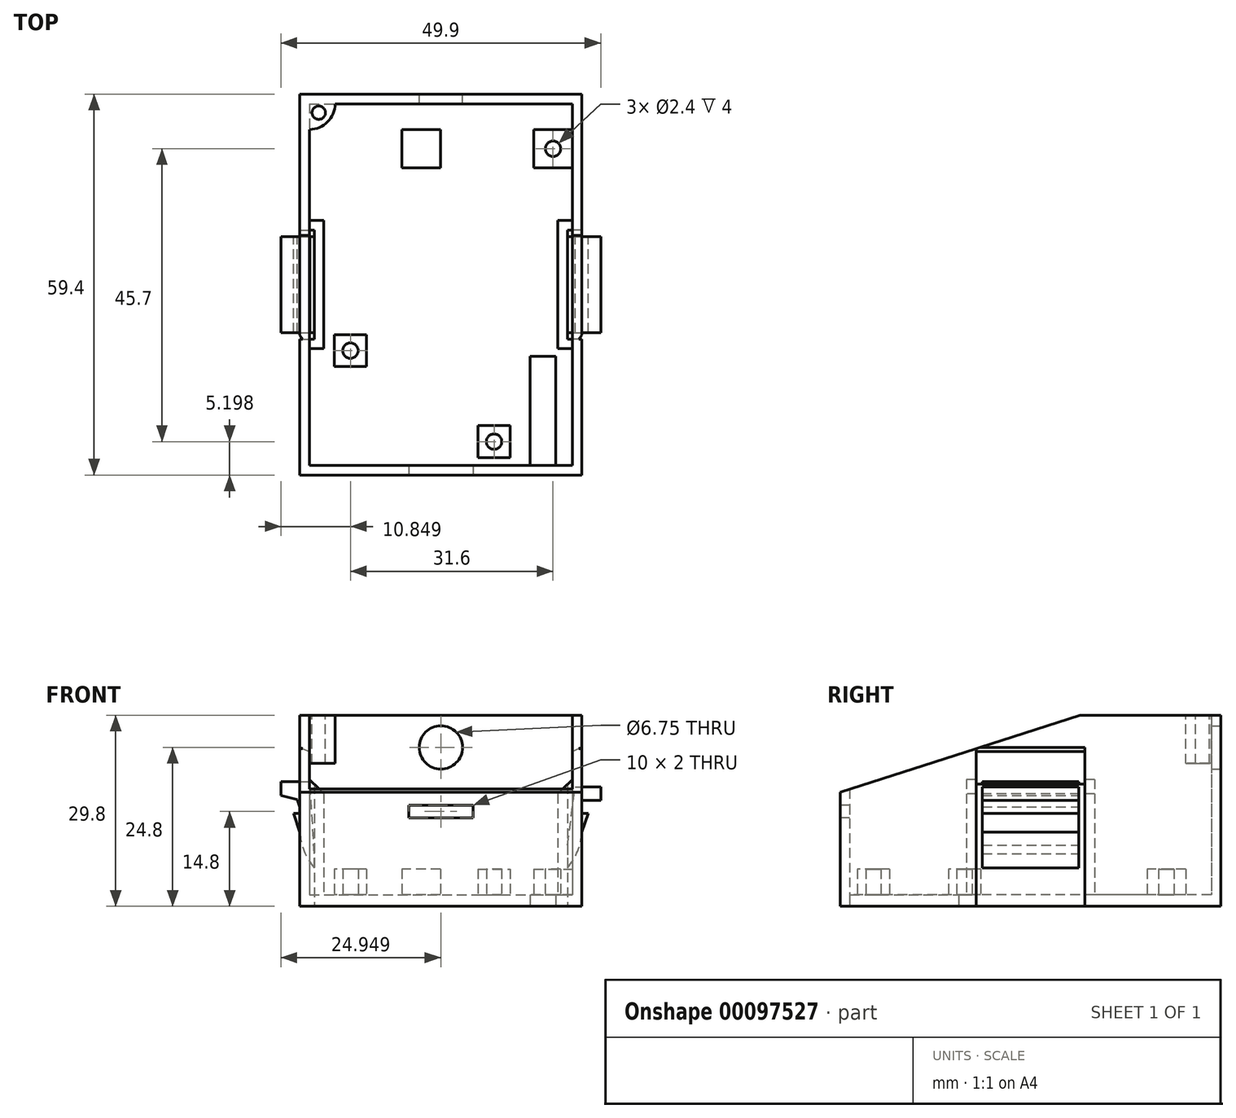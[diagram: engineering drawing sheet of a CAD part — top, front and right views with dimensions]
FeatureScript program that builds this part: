
annotation { "Feature Type Name" : "Feature", "Feature Type Description" : "" }
export const myFeature = defineFeature(function(context is Context, id is Id, definition is map)
    precondition{}
    {
        {
            var Q0;
            Q0=qCreatedBy(makeId("Top.planeOp"),FACE);
            var sketch = newSketch(context, id + "F0", { "sketchPlane" : qUnion([Q0])});
            skLineSegment(sketch, "E0.bottom", {"start": v(-56.63, 54.28) * mm, "end": v(-12.63, 54.28) * mm});
            skLineSegment(sketch, "E0.top", {"start": v(-56.63, -5.12) * mm, "end": v(-12.63, -5.12) * mm});
            skCircle(sketch, "E1", {"center": v(-12.63, -5.12) * mm, "radius": 1.5 * mm, "construction": true});
            skCircle(sketch, "E2", {"center": v(-56.63, -5.12) * mm, "radius": 1.5 * mm, "construction": true});
            skLineSegment(sketch, "E3", {"start": v(-56.63, -3.62) * mm, "end": v(-12.63, -3.62) * mm, "construction": true});
            skCircle(sketch, "E4", {"center": v(-12.63, -3.62) * mm, "radius": 4.1 * mm, "construction": true});
            skLineSegment(sketch, "E5.bottom", {"start": v(-16.73, -3.62) * mm, "end": v(-20.73, -3.62) * mm});
            skLineSegment(sketch, "E5.top", {"start": v(-16.73, 13.38) * mm, "end": v(-20.73, 13.38) * mm});
            skLineSegment(sketch, "E5.left", {"start": v(-16.73, -3.62) * mm, "end": v(-16.73, 13.38) * mm});
            skLineSegment(sketch, "E5.right", {"start": v(-20.73, -3.62) * mm, "end": v(-20.73, 13.38) * mm});
            skLineSegment(sketch, "E6", {"start": v(-56.63, 24.58) * mm, "end": v(-12.63, 24.58) * mm, "construction": true});
            skCircle(sketch, "E7", {"center": v(-56.63, 24.58) * mm, "radius": 8.5 * mm, "construction": true});
            skLineSegment(sketch, "E8", {"start": v(-56.63, 33.08) * mm, "end": v(-54.38, 33.08) * mm});
            skLineSegment(sketch, "E9", {"start": v(-56.63, 16.08) * mm, "end": v(-54.38, 16.08) * mm});
            skLineSegment(sketch, "E10", {"start": v(-54.38, 33.08) * mm, "end": v(-54.38, 16.08) * mm});
            skLineSegment(sketch, "E11", {"start": v(-56.63, 54.28) * mm, "end": v(-56.63, 33.08) * mm});
            skLineSegment(sketch, "E12", {"start": v(-56.63, 16.08) * mm, "end": v(-56.63, -5.12) * mm});
            skLineSegment(sketch, "E13", {"start": v(-34.63, 54.28) * mm, "end": v(-34.63, 40.65) * mm, "construction": true});
            skLineSegment(sketch, "E14.MirrorCS", {"start": v(-12.63, 16.08) * mm, "end": v(-12.63, -5.12) * mm});
            skLineSegment(sketch, "E15.MirrorCS", {"start": v(-12.63, 16.08) * mm, "end": v(-14.88, 16.08) * mm});
            skLineSegment(sketch, "E16.MirrorCS", {"start": v(-12.63, 33.08) * mm, "end": v(-14.88, 33.08) * mm});
            skLineSegment(sketch, "E17.MirrorCS", {"start": v(-12.63, 54.28) * mm, "end": v(-12.63, 33.08) * mm});
            skLineSegment(sketch, "E18.MirrorCS", {"start": v(-14.88, 33.08) * mm, "end": v(-14.88, 16.08) * mm});
            skSolve(sketch);
        }
        {
            var Q0;
            Q0=makeQuery(id+"F0.imprint","IMPRINT",FACE,{"disambiguationData":[TD([[makeQuery(id+"F0.imprint","IMPRINT",EDGE,{"derivedFrom":sQuery(id+"F0.wireOp",EDGE,"E0.bottom")}),-1.0]])]});
            extrude(context, id + "F1", {"entities" : qUnion([Q0]), "depth" : 1.8 * mm});
        }
        {
            var Q0;
            Q0=makeQuery(id+"F1.opExtrude","CAP_FACE",FACE,{"disambiguationData":[OSD([sQuery(id+"F0.wireOp",EDGE,"E0.bottom"),sQuery(id+"F0.wireOp",EDGE,"E0.top"),sQuery(id+"F0.wireOp",EDGE,"E5.bottom"),sQuery(id+"F0.wireOp",EDGE,"E5.top"),sQuery(id+"F0.wireOp",EDGE,"E5.left"),sQuery(id+"F0.wireOp",EDGE,"E5.right"),sQuery(id+"F0.wireOp",EDGE,"E8"),sQuery(id+"F0.wireOp",EDGE,"E9"),sQuery(id+"F0.wireOp",EDGE,"E10"),sQuery(id+"F0.wireOp",EDGE,"E11"),sQuery(id+"F0.wireOp",EDGE,"E12"),sQuery(id+"F0.wireOp",EDGE,"E14.MirrorCS"),sQuery(id+"F0.wireOp",EDGE,"E15.MirrorCS"),sQuery(id+"F0.wireOp",EDGE,"E16.MirrorCS"),sQuery(id+"F0.wireOp",EDGE,"E17.MirrorCS"),sQuery(id+"F0.wireOp",EDGE,"E18.MirrorCS")])],"isStart":false});
            var sketch = newSketch(context, id + "F2", { "sketchPlane" : qUnion([Q0])});
            skLineSegment(sketch, "E19.0", {"start": v(-55.13, 52.78) * mm, "end": v(-55.13, 34.58) * mm});
            skLineSegment(sketch, "E19.1", {"start": v(-14.13, 14.58) * mm, "end": v(-16.38, 14.58) * mm});
            skLineSegment(sketch, "E19.2", {"start": v(-16.38, 34.58) * mm, "end": v(-16.38, 14.58) * mm});
            skLineSegment(sketch, "E19.3", {"start": v(-14.13, 34.58) * mm, "end": v(-16.38, 34.58) * mm});
            skLineSegment(sketch, "E19.4", {"start": v(-14.13, 52.78) * mm, "end": v(-14.13, 34.58) * mm});
            skLineSegment(sketch, "E19.5", {"start": v(-14.13, 14.58) * mm, "end": v(-14.13, -3.62) * mm});
            skLineSegment(sketch, "E19.6", {"start": v(-55.13, 52.78) * mm, "end": v(-14.13, 52.78) * mm});
            skLineSegment(sketch, "E19.7", {"start": v(-55.13, -3.62) * mm, "end": v(-14.13, -3.62) * mm});
            skLineSegment(sketch, "E19.8", {"start": v(-55.13, 14.58) * mm, "end": v(-55.13, -3.62) * mm});
            skLineSegment(sketch, "E19.9", {"start": v(-55.13, 14.58) * mm, "end": v(-52.88, 14.58) * mm});
            skLineSegment(sketch, "E19.10", {"start": v(-52.88, 34.58) * mm, "end": v(-52.88, 14.58) * mm});
            skLineSegment(sketch, "E19.11", {"start": v(-55.13, 34.58) * mm, "end": v(-52.88, 34.58) * mm});
            skSolve(sketch);
        }
        {
            var Q0;
            Q0=makeQuery(id+"F2.imprint","IMPRINT",FACE,{"disambiguationData":[TD([[makeQuery(id+"F2.imprint","IMPRINT",EDGE,{"derivedFrom":sQuery(id+"F2.wireOp",EDGE,"E19.0")}),-1.0]])]});
            extrude(context, id + "F3", {"entities" : qUnion([Q0]), "operationType" : NewBodyOperationType.ADD, "depth" : 22 * mm});
        }
        {
            var Q0;
            Q0=makeQuery(id+"F3.opExtrude","CAP_FACE",FACE,{"disambiguationData":[OSD([sQuery(id+"F0.wireOp",EDGE,"E0.bottom"),sQuery(id+"F0.wireOp",EDGE,"E0.top"),sQuery(id+"F0.wireOp",EDGE,"E8"),sQuery(id+"F0.wireOp",EDGE,"E9"),sQuery(id+"F0.wireOp",EDGE,"E10"),sQuery(id+"F0.wireOp",EDGE,"E11"),sQuery(id+"F0.wireOp",EDGE,"E12"),sQuery(id+"F0.wireOp",EDGE,"E14.MirrorCS"),sQuery(id+"F0.wireOp",EDGE,"E15.MirrorCS"),sQuery(id+"F0.wireOp",EDGE,"E16.MirrorCS"),sQuery(id+"F0.wireOp",EDGE,"E17.MirrorCS"),sQuery(id+"F0.wireOp",EDGE,"E18.MirrorCS"),sQuery(id+"F2.wireOp",EDGE,"E19.0"),sQuery(id+"F2.wireOp",EDGE,"E19.1"),sQuery(id+"F2.wireOp",EDGE,"E19.2"),sQuery(id+"F2.wireOp",EDGE,"E19.3"),sQuery(id+"F2.wireOp",EDGE,"E19.4"),sQuery(id+"F2.wireOp",EDGE,"E19.5"),sQuery(id+"F2.wireOp",EDGE,"E19.6"),sQuery(id+"F2.wireOp",EDGE,"E19.7"),sQuery(id+"F2.wireOp",EDGE,"E19.8"),sQuery(id+"F2.wireOp",EDGE,"E19.9"),sQuery(id+"F2.wireOp",EDGE,"E19.10"),sQuery(id+"F2.wireOp",EDGE,"E19.11")])],"isStart":false});
            var sketch = newSketch(context, id + "F4", { "sketchPlane" : qUnion([Q0])});
            skLineSegment(sketch, "E20.bottom", {"start": v(-56.63, 54.28) * mm, "end": v(-12.63, 54.28) * mm});
            skLineSegment(sketch, "E20.top", {"start": v(-56.63, -5.12) * mm, "end": v(-12.63, -5.12) * mm});
            skLineSegment(sketch, "E20.left", {"start": v(-56.63, 54.28) * mm, "end": v(-56.63, -5.12) * mm});
            skLineSegment(sketch, "E20.right", {"start": v(-12.63, 54.28) * mm, "end": v(-12.63, -5.12) * mm});
            skLineSegment(sketch, "E21.bottom", {"start": v(-55.13, 52.78) * mm, "end": v(-14.13, 52.78) * mm});
            skLineSegment(sketch, "E21.top", {"start": v(-55.13, -3.62) * mm, "end": v(-14.13, -3.62) * mm});
            skLineSegment(sketch, "E22", {"start": v(-14.13, 52.78) * mm, "end": v(-55.13, 52.78) * mm});
            skLineSegment(sketch, "E23", {"start": v(-55.13, 52.78) * mm, "end": v(-55.13, 34.58) * mm});
            skLineSegment(sketch, "E24", {"start": v(-55.13, 34.58) * mm, "end": v(-52.88, 34.58) * mm});
            skLineSegment(sketch, "E25", {"start": v(-52.88, 34.58) * mm, "end": v(-52.88, 14.58) * mm});
            skLineSegment(sketch, "E26", {"start": v(-52.88, 14.58) * mm, "end": v(-55.13, 14.58) * mm});
            skLineSegment(sketch, "E27", {"start": v(-55.13, 14.58) * mm, "end": v(-55.13, -3.62) * mm});
            skLineSegment(sketch, "E28", {"start": v(-14.13, -3.62) * mm, "end": v(-14.13, 14.58) * mm});
            skLineSegment(sketch, "E29", {"start": v(-14.13, 14.58) * mm, "end": v(-16.38, 14.58) * mm});
            skLineSegment(sketch, "E30", {"start": v(-16.38, 14.58) * mm, "end": v(-16.38, 34.58) * mm});
            skLineSegment(sketch, "E31", {"start": v(-16.38, 34.58) * mm, "end": v(-14.13, 34.58) * mm});
            skLineSegment(sketch, "E32", {"start": v(-14.13, 34.58) * mm, "end": v(-14.13, 52.78) * mm});
            skSolve(sketch);
        }
        {
            var Q0;
            Q0=qSketchRegion(id+"F4",true);
            extrude(context, id + "F5", {"entities" : qUnion([Q0]), "operationType" : NewBodyOperationType.ADD, "depth" : 6 * mm});
        }
        {
            var Q0;
            Q0=makeQuery(id+"F5.opExtrude","CAP_FACE",FACE,{"disambiguationData":[OSD([sQuery(id+"F4.wireOp",EDGE,"E20.bottom"),sQuery(id+"F4.wireOp",EDGE,"E20.top"),sQuery(id+"F4.wireOp",EDGE,"E20.left"),sQuery(id+"F4.wireOp",EDGE,"E20.right"),sQuery(id+"F4.wireOp",EDGE,"E21.top"),sQuery(id+"F4.wireOp",EDGE,"E22"),sQuery(id+"F4.wireOp",EDGE,"E23"),sQuery(id+"F4.wireOp",EDGE,"E24"),sQuery(id+"F4.wireOp",EDGE,"E25"),sQuery(id+"F4.wireOp",EDGE,"E26"),sQuery(id+"F4.wireOp",EDGE,"E27"),sQuery(id+"F4.wireOp",EDGE,"E28"),sQuery(id+"F4.wireOp",EDGE,"E29"),sQuery(id+"F4.wireOp",EDGE,"E30"),sQuery(id+"F4.wireOp",EDGE,"E31"),sQuery(id+"F4.wireOp",EDGE,"E32")])],"isStart":false});
            var sketch = newSketch(context, id + "F6", { "sketchPlane" : qUnion([Q0])});
            skLineSegment(sketch, "E33.bottom", {"start": v(-55.13, 34.58) * mm, "end": v(-52.88, 34.58) * mm});
            skLineSegment(sketch, "E33.top", {"start": v(-55.13, 14.58) * mm, "end": v(-52.88, 14.58) * mm});
            skLineSegment(sketch, "E33.left", {"start": v(-55.13, 34.58) * mm, "end": v(-55.13, 14.58) * mm});
            skLineSegment(sketch, "E33.right", {"start": v(-52.88, 34.58) * mm, "end": v(-52.88, 14.58) * mm});
            skLineSegment(sketch, "E34.bottom", {"start": v(-16.38, 34.58) * mm, "end": v(-14.13, 34.58) * mm});
            skLineSegment(sketch, "E34.top", {"start": v(-16.38, 14.58) * mm, "end": v(-14.13, 14.58) * mm});
            skLineSegment(sketch, "E34.left", {"start": v(-16.38, 34.58) * mm, "end": v(-16.38, 14.58) * mm});
            skLineSegment(sketch, "E34.right", {"start": v(-14.13, 34.58) * mm, "end": v(-14.13, 14.58) * mm});
            skSolve(sketch);
        }
        {
            var Q0;
            Q0=qSketchRegion(id+"F6",true);
            extrude(context, id + "F7", {"entities" : qUnion([Q0]), "operationType" : NewBodyOperationType.REMOVE, "oppositeDirection" : true, "depth" : 10 * mm});
        }
        {
            var Q0;
            Q0=makeQuery(id+"F5.boolean.opBoolean","MERGE",FACE,{"derivedFrom":[makeQuery(id+"F3.opExtrude","SWEPT_FACE",FACE,{"disambiguationData":[OSD([sQuery(id+"F2.wireOp",EDGE,"E19.9")])]}),makeQuery(id+"F5.opExtrude","SWEPT_FACE",FACE,{"disambiguationData":[OSD([sQuery(id+"F4.wireOp",EDGE,"E26")])]})]});
            var sketch = newSketch(context, id + "F8", { "sketchPlane" : qUnion([Q0])});
            skLineSegment(sketch, "E35", {"start": v(-55.13, 19.8) * mm, "end": v(-52.88, 17.55) * mm});
            skLineSegment(sketch, "E36", {"start": v(-52.88, 17.55) * mm, "end": v(-52.88, 19.8) * mm});
            skLineSegment(sketch, "E37", {"start": v(-52.88, 19.8) * mm, "end": v(-55.13, 19.8) * mm});
            skSolve(sketch);
        }
        {
            var Q0;
            Q0=makeQuery(id+"F8.imprint","IMPRINT",FACE,{"disambiguationData":[TD([[makeQuery(id+"F8.imprint","IMPRINT",EDGE,{"derivedFrom":sQuery(id+"F8.wireOp",EDGE,"E35")}),1.0]])]});
            extrude(context, id + "F9", {"entities" : qUnion([Q0]), "operationType" : NewBodyOperationType.REMOVE, "oppositeDirection" : true, "depth" : 20 * mm});
        }
        {
            var Q0;
            {var subQ0=sQuery(id+"F0.wireOp",EDGE,"E8");Q0=makeQuery(id+"F3.boolean.opBoolean","MERGE",FACE,{"derivedFrom":[makeQuery(id+"F1.opExtrude","SWEPT_FACE",FACE,{"disambiguationData":[OSD([subQ0])]}),makeQuery(id+"F3.opExtrude","SWEPT_FACE",FACE,{"disambiguationData":[OSD([subQ0])]})]});}
            var sketch = newSketch(context, id + "F10", { "sketchPlane" : qUnion([Q0])});
            skLineSegment(sketch, "E38", {"start": v(-56.63, 23.8) * mm, "end": v(-54.38, 23.8) * mm});
            skLineSegment(sketch, "E39", {"start": v(-56.63, 23.8) * mm, "end": v(-56.63, 24.8) * mm});
            skLineSegment(sketch, "E40", {"start": v(-56.63, 23.8) * mm, "end": v(-55.88, 23.8) * mm});
            skCircle(sketch, "E41", {"center": v(-56.63, 23.8) * mm, "radius": 2 * mm, "construction": true});
            skLineSegment(sketch, "E42", {"start": v(-56.63, 24.8) * mm, "end": v(-54.38, 23.8) * mm});
            skSolve(sketch);
        }
        {
            var Q0;
            Q0=qSketchRegion(id+"F10",true);
            extrude(context, id + "F11", {"entities" : qUnion([Q0]), "operationType" : NewBodyOperationType.REMOVE, "depth" : 17 * mm});
        }
        {
            var Q0;
            Q0=makeQuery(id+"F5.boolean.opBoolean","MERGE",FACE,{"derivedFrom":[makeQuery(id+"F3.opExtrude","SWEPT_FACE",FACE,{"disambiguationData":[OSD([sQuery(id+"F2.wireOp",EDGE,"E19.3")])]}),makeQuery(id+"F5.opExtrude","SWEPT_FACE",FACE,{"disambiguationData":[OSD([sQuery(id+"F4.wireOp",EDGE,"E31")])]})]});
            var sketch = newSketch(context, id + "F12", { "sketchPlane" : qUnion([Q0])});
            skLineSegment(sketch, "E43", {"start": v(16.38, 19.8) * mm, "end": v(14.13, 19.8) * mm});
            skLineSegment(sketch, "E44", {"start": v(14.13, 19.8) * mm, "end": v(16.38, 17.55) * mm});
            skLineSegment(sketch, "E45", {"start": v(16.38, 17.55) * mm, "end": v(16.38, 19.8) * mm});
            skSolve(sketch);
        }
        {
            var Q0;
            Q0=qSketchRegion(id+"F12",true);
            extrude(context, id + "F13", {"entities" : qUnion([Q0]), "operationType" : NewBodyOperationType.REMOVE, "oppositeDirection" : true, "depth" : 20 * mm});
        }
        {
            var Q0;
            {var subQ0=sQuery(id+"F0.wireOp",EDGE,"E15.MirrorCS");Q0=makeQuery(id+"F3.boolean.opBoolean","MERGE",FACE,{"derivedFrom":[makeQuery(id+"F1.opExtrude","SWEPT_FACE",FACE,{"disambiguationData":[OSD([subQ0])]}),makeQuery(id+"F3.opExtrude","SWEPT_FACE",FACE,{"disambiguationData":[OSD([subQ0])]})]});}
            var sketch = newSketch(context, id + "F14", { "sketchPlane" : qUnion([Q0])});
            skLineSegment(sketch, "E46", {"start": v(12.63, 23.8) * mm, "end": v(12.63, 24.8) * mm});
            skLineSegment(sketch, "E47", {"start": v(12.63, 24.8) * mm, "end": v(14.88, 23.8) * mm});
            skLineSegment(sketch, "E48", {"start": v(14.88, 23.8) * mm, "end": v(12.63, 23.8) * mm});
            skSolve(sketch);
        }
        {
            var Q0;
            Q0=qSketchRegion(id+"F14",true);
            extrude(context, id + "F15", {"entities" : qUnion([Q0]), "operationType" : NewBodyOperationType.REMOVE, "depth" : 17 * mm});
        }
        {
            var Q0;
            {var subQ0=sQuery(id+"F0.wireOp",EDGE,"E17.MirrorCS");var subQ1=sQuery(id+"F0.wireOp",EDGE,"E14.MirrorCS");Q0=makeQuery(id+"F5.boolean.opBoolean","MERGE",FACE,{"derivedFrom":[makeQuery(id+"F3.boolean.opBoolean","MERGE",FACE,{"derivedFrom":[makeQuery(id+"F1.opExtrude","SWEPT_FACE",FACE,{"disambiguationData":[OSD([subQ1])]}),makeQuery(id+"F3.opExtrude","SWEPT_FACE",FACE,{"disambiguationData":[OSD([subQ1])]})]}),makeQuery(id+"F3.boolean.opBoolean","MERGE",FACE,{"derivedFrom":[makeQuery(id+"F1.opExtrude","SWEPT_FACE",FACE,{"disambiguationData":[OSD([subQ0])]}),makeQuery(id+"F3.opExtrude","SWEPT_FACE",FACE,{"disambiguationData":[OSD([subQ0])]})]}),makeQuery(id+"F5.opExtrude","SWEPT_FACE",FACE,{"disambiguationData":[OSD([sQuery(id+"F4.wireOp",EDGE,"E20.right")])]})]});}
            var sketch = newSketch(context, id + "F16", { "sketchPlane" : qUnion([Q0])});
            skCircle(sketch, "E49", {"center": v(-5.12, 29.8) * mm, "radius": 12 * mm, "construction": true});
            skCircle(sketch, "E50", {"center": v(54.28, 29.8) * mm, "radius": 22 * mm, "construction": true});
            skLineSegment(sketch, "E51", {"start": v(-5.12, 29.8) * mm, "end": v(-5.12, 17.8) * mm});
            skLineSegment(sketch, "E52", {"start": v(-5.12, 17.8) * mm, "end": v(32.28, 29.8) * mm});
            skLineSegment(sketch, "E53", {"start": v(32.28, 29.8) * mm, "end": v(-5.12, 29.8) * mm});
            skCircle(sketch, "E54", {"center": v(54.28, 29.8) * mm, "radius": 10 * mm, "construction": true});
            skLineSegment(sketch, "E55", {"start": v(44.28, 29.8) * mm, "end": v(44.28, 23.8) * mm, "construction": true});
            skCircle(sketch, "E56", {"center": v(44.28, 23.8) * mm, "radius": 3.38 * mm, "construction": true});
            skSolve(sketch);
        }
        {
            var Q0;
            Q0=qSketchRegion(id+"F16",true);
            extrude(context, id + "F17", {"entities" : qUnion([Q0]), "operationType" : NewBodyOperationType.REMOVE, "oppositeDirection" : true, "depth" : 45 * mm});
        }
        {
            var Q0;
            {var subQ0=sQuery(id+"F0.wireOp",EDGE,"E0.bottom");Q0=makeQuery(id+"F5.boolean.opBoolean","MERGE",FACE,{"derivedFrom":[makeQuery(id+"F3.boolean.opBoolean","MERGE",FACE,{"derivedFrom":[makeQuery(id+"F1.opExtrude","SWEPT_FACE",FACE,{"disambiguationData":[OSD([subQ0])]}),makeQuery(id+"F3.opExtrude","SWEPT_FACE",FACE,{"disambiguationData":[OSD([subQ0])]})]}),makeQuery(id+"F5.opExtrude","SWEPT_FACE",FACE,{"disambiguationData":[OSD([sQuery(id+"F4.wireOp",EDGE,"E20.bottom")])]})]});}
            var sketch = newSketch(context, id + "F18", { "sketchPlane" : qUnion([Q0])});
            skLineSegment(sketch, "E57", {"start": v(34.63, 29.8) * mm, "end": v(34.63, 24.8) * mm, "construction": true});
            skCircle(sketch, "E58", {"center": v(34.63, 24.8) * mm, "radius": 3.38 * mm});
            skSolve(sketch);
        }
        {
            var Q0;
            Q0=qSketchRegion(id+"F18",true);
            extrude(context, id + "F19", {"entities" : qUnion([Q0]), "operationType" : NewBodyOperationType.REMOVE, "oppositeDirection" : true, "depth" : 3 * mm});
        }
        {
            var Q0;
            Q0=makeQuery(id+"F5.opExtrude","CAP_FACE",FACE,{"disambiguationData":[OSD([sQuery(id+"F4.wireOp",EDGE,"E20.bottom"),sQuery(id+"F4.wireOp",EDGE,"E20.top"),sQuery(id+"F4.wireOp",EDGE,"E20.left"),sQuery(id+"F4.wireOp",EDGE,"E20.right"),sQuery(id+"F4.wireOp",EDGE,"E21.top"),sQuery(id+"F4.wireOp",EDGE,"E22"),sQuery(id+"F4.wireOp",EDGE,"E23"),sQuery(id+"F4.wireOp",EDGE,"E24"),sQuery(id+"F4.wireOp",EDGE,"E25"),sQuery(id+"F4.wireOp",EDGE,"E26"),sQuery(id+"F4.wireOp",EDGE,"E27"),sQuery(id+"F4.wireOp",EDGE,"E28"),sQuery(id+"F4.wireOp",EDGE,"E29"),sQuery(id+"F4.wireOp",EDGE,"E30"),sQuery(id+"F4.wireOp",EDGE,"E31"),sQuery(id+"F4.wireOp",EDGE,"E32")])],"isStart":false});
            var sketch = newSketch(context, id + "F20", { "sketchPlane" : qUnion([Q0])});
            skArc(sketch, "E59", {"start": v(-55.13, 48.78) * mm, "mid": v(-52.3, 49.96) * mm, "end": v(-51.13, 52.78) * mm});
            skLineSegment(sketch, "E60", {"start": v(-55.13, 52.78) * mm, "end": v(-52.23, 50.04) * mm, "construction": true});
            skLineSegment(sketch, "E61", {"start": v(-34.63, 54.28) * mm, "end": v(-34.63, 59.78) * mm, "construction": true});
            skCircle(sketch, "E62", {"center": v(-53.68, 51.4) * mm, "radius": 1.05 * mm});
            skArc(sketch, "E63.MirrorCS", {"start": v(-14.13, 48.78) * mm, "mid": v(-16.95, 49.96) * mm, "end": v(-18.13, 52.78) * mm});
            skCircle(sketch, "E64.MirrorC", {"center": v(-15.58, 51.4) * mm, "radius": 1.05 * mm});
            skSolve(sketch);
        }
        {
            var Q0;
            {var subQ0=sQuery(id+"F20.wireOp",EDGE,"E59");Q0=makeQuery(id+"F20.imprint","IMPRINT",FACE,{"disambiguationData":[TD([[makeQuery(id+"F20.imprint","IMPRINT",EDGE,{"derivedFrom":subQ0}),1.0]])]});}
            var Q1;
            {var subQ0=sQuery(id+"F20.wireOp",EDGE,"E63.MirrorCS");Q1=makeQuery(id+"F20.imprint","IMPRINT",FACE,{"disambiguationData":[TD([[makeQuery(id+"F20.imprint","IMPRINT",EDGE,{"derivedFrom":subQ0}),-1.0]])]});}
            extrude(context, id + "F21", {"entities" : qUnion([Q0, Q1]), "operationType" : NewBodyOperationType.ADD, "oppositeDirection" : true, "depth" : 7.5 * mm});
        }
        {
            var Q0;
            {var subQ0=sQuery(id+"F0.wireOp",EDGE,"E0.top");Q0=makeQuery(id+"F5.boolean.opBoolean","MERGE",FACE,{"derivedFrom":[makeQuery(id+"F3.boolean.opBoolean","MERGE",FACE,{"derivedFrom":[makeQuery(id+"F1.opExtrude","SWEPT_FACE",FACE,{"disambiguationData":[OSD([subQ0])]}),makeQuery(id+"F3.opExtrude","SWEPT_FACE",FACE,{"disambiguationData":[OSD([subQ0])]})]}),makeQuery(id+"F5.opExtrude","SWEPT_FACE",FACE,{"disambiguationData":[OSD([sQuery(id+"F4.wireOp",EDGE,"E20.top")])]})]});}
            var sketch = newSketch(context, id + "F22", { "sketchPlane" : qUnion([Q0])});
            skCircle(sketch, "E65", {"center": v(-56.63, 17.8) * mm, "radius": 2 * mm, "construction": true});
            skLineSegment(sketch, "E66", {"start": v(-56.63, 15.8) * mm, "end": v(-12.63, 15.8) * mm, "construction": true});
            skCircle(sketch, "E67", {"center": v(-34.63, 15.8) * mm, "radius": 5 * mm, "construction": true});
            skLineSegment(sketch, "E68", {"start": v(-29.63, 15.8) * mm, "end": v(-29.63, 13.8) * mm});
            skLineSegment(sketch, "E69.bottom", {"start": v(-29.63, 13.8) * mm, "end": v(-39.63, 13.8) * mm});
            skLineSegment(sketch, "E69.top", {"start": v(-29.63, 15.8) * mm, "end": v(-39.63, 15.8) * mm});
            skLineSegment(sketch, "E69.left", {"start": v(-29.63, 13.8) * mm, "end": v(-29.63, 15.8) * mm});
            skLineSegment(sketch, "E69.right", {"start": v(-39.63, 13.8) * mm, "end": v(-39.63, 15.8) * mm});
            skSolve(sketch);
        }
        {
            var Q0;
            Q0=qSketchRegion(id+"F22",true);
            extrude(context, id + "F23", {"entities" : qUnion([Q0]), "operationType" : NewBodyOperationType.REMOVE, "oppositeDirection" : true, "depth" : 2.5 * mm});
        }
        {
            var Q0;
            {var subQ0=sQuery(id+"F0.wireOp",EDGE,"E16.MirrorCS");Q0=makeQuery(id+"F15.boolean.opBoolean","MERGE",FACE,{"derivedFrom":[makeQuery(id+"F3.boolean.opBoolean","MERGE",FACE,{"derivedFrom":[makeQuery(id+"F1.opExtrude","SWEPT_FACE",FACE,{"disambiguationData":[OSD([subQ0])]}),makeQuery(id+"F3.opExtrude","SWEPT_FACE",FACE,{"disambiguationData":[OSD([subQ0])]})]}),makeQuery(id+"F15.opExtrude","CAP_FACE",FACE,{"disambiguationData":[OSD([sQuery(id+"F14.wireOp",EDGE,"E46"),sQuery(id+"F14.wireOp",EDGE,"E47"),sQuery(id+"F14.wireOp",EDGE,"E48")])],"isStart":false})]});}
            var sketch = newSketch(context, id + "F24", { "sketchPlane" : qUnion([Q0])});
            skLineSegment(sketch, "E70", {"start": v(-14.88, 0) * mm, "end": v(-14.88, 6) * mm, "construction": true});
            skCircle(sketch, "E71", {"center": v(-14.88, 6) * mm, "radius": 6 * mm, "construction": true});
            skArc(sketch, "E72", {"start": v(-14.88, 6) * mm, "mid": v(-13.3, 8.6) * mm, "end": v(-12.63, 11.56) * mm});
            skCircle(sketch, "E73", {"center": v(-14.88, 9.52) * mm, "radius": 5 * mm, "construction": true});
            skLineSegment(sketch, "E74", {"start": v(-14.88, 14.52) * mm, "end": v(-5.95, 14.52) * mm, "construction": true});
            skCircle(sketch, "E75", {"center": v(-12.63, 14.52) * mm, "radius": 1 * mm, "construction": true});
            skLineSegment(sketch, "E76", {"start": v(-12.63, 11.56) * mm, "end": v(-11.63, 14.52) * mm});
            skCircle(sketch, "E77", {"center": v(-14.88, 14.52) * mm, "radius": 1.2 * mm, "construction": true});
            skLineSegment(sketch, "E78", {"start": v(-13.68, 18.62) * mm, "end": v(-9.68, 18.62) * mm});
            skLineSegment(sketch, "E79", {"start": v(-11.63, 14.52) * mm, "end": v(-12.63, 14.52) * mm});
            skCircle(sketch, "E80", {"center": v(-12.63, 14.52) * mm, "radius": 2 * mm, "construction": true});
            skLineSegment(sketch, "E81", {"start": v(-12.63, 14.52) * mm, "end": v(-12.63, 16.52) * mm});
            skLineSegment(sketch, "E82", {"start": v(-12.63, 16.52) * mm, "end": v(-9.68, 16.52) * mm});
            skLineSegment(sketch, "E83", {"start": v(-14.88, 9.52) * mm, "end": v(-13.68, 18.62) * mm});
            skLineSegment(sketch, "E84", {"start": v(-9.68, 18.62) * mm, "end": v(-9.68, 16.52) * mm});
            skLineSegment(sketch, "E85", {"start": v(-12.63, 6.02) * mm, "end": v(-56.63, 6.02) * mm, "construction": true});
            skLineSegment(sketch, "E86", {"start": v(-34.63, 6.02) * mm, "end": v(-34.63, 12.32) * mm, "construction": true});
            skCircle(sketch, "E87.MirrorC", {"center": v(-56.63, 14.52) * mm, "radius": 2 * mm, "construction": true});
            skLineSegment(sketch, "E88.MirrorCS", {"start": v(-56.63, 11.56) * mm, "end": v(-57.63, 14.53) * mm});
            skArc(sketch, "E89.MirrorCS", {"start": v(-54.38, 6) * mm, "mid": v(-55.96, 8.6) * mm, "end": v(-56.63, 11.56) * mm});
            skLineSegment(sketch, "E90.MirrorCS", {"start": v(-57.63, 14.52) * mm, "end": v(-56.63, 14.52) * mm});
            skLineSegment(sketch, "E91", {"start": v(-14.88, 9.52) * mm, "end": v(-14.88, 6) * mm});
            skCircle(sketch, "E92", {"center": v(-56.63, 16.52) * mm, "radius": 0.8 * mm, "construction": true});
            skPoint(sketch, "E93.endSnap0", {"position": v(-56.63, 15.52) * mm});
            skLineSegment(sketch, "E94", {"start": v(-56.63, 17.32) * mm, "end": v(-59.88, 17.32) * mm, "construction": true});
            skLineSegment(sketch, "E95", {"start": v(-59.58, 17.32) * mm, "end": v(-59.58, 19.42) * mm});
            skLineSegment(sketch, "E96", {"start": v(-59.58, 17.32) * mm, "end": v(-57.03, 16.63) * mm});
            skLineSegment(sketch, "E97", {"start": v(-56.63, 14.52) * mm, "end": v(-56.63, 15.52) * mm});
            skLineSegment(sketch, "E98", {"start": v(-56.63, 15.52) * mm, "end": v(-57.03, 16.63) * mm});
            skLineSegment(sketch, "E99", {"start": v(-59.58, 19.42) * mm, "end": v(-55.04, 19.42) * mm});
            skLineSegment(sketch, "E100", {"start": v(-54.38, 6) * mm, "end": v(-54.38, 8.23) * mm});
            skLineSegment(sketch, "E101", {"start": v(-54.38, 8.23) * mm, "end": v(-55.04, 19.42) * mm});
            skSolve(sketch);
        }
        {
            var Q0;
            Q0=makeQuery(id+"F24.imprint","IMPRINT",FACE,{"disambiguationData":[TD([[makeQuery(id+"F24.imprint","IMPRINT",EDGE,{"derivedFrom":sQuery(id+"F24.wireOp",EDGE,"3a5f83b2-c532-4f29-86cb-ad45a0fee2c30.MirrorCS")}),1.0]])]});
            var Q1;
            {var subQ6=sQuery(id+"F24.wireOp",EDGE,"E82");Q1=makeQuery(id+"F24.imprint","IMPRINT",FACE,{"disambiguationData":[TD([[makeQuery(id+"F24.imprint","IMPRINT",EDGE,{"derivedFrom":subQ6}),1.0]])]});}
            var Q2;
            {var subQ7=sQuery(id+"F24.wireOp",EDGE,"E72");Q2=makeQuery(id+"F24.imprint","IMPRINT",FACE,{"disambiguationData":[TD([[makeQuery(id+"F24.imprint","IMPRINT",EDGE,{"derivedFrom":subQ7}),1.0]])]});}
            var Q3;
            {var subQ0=sQuery(id+"F24.wireOp",EDGE,"E76");Q3=makeQuery(id+"F24.imprint","IMPRINT",FACE,{"disambiguationData":[TD([[makeQuery(id+"F24.imprint","IMPRINT",EDGE,{"derivedFrom":subQ0}),1.0]])]});}
            var Q4;
            Q4=makeQuery(id+"F24.imprint","IMPRINT",FACE,{"disambiguationData":[TD([[makeQuery(id+"F24.imprint","IMPRINT",EDGE,{"derivedFrom":sQuery(id+"F24.wireOp",EDGE,"E88.MirrorCS")}),-1.0]])]});
            extrude(context, id + "F25", {"entities" : qUnion([Q0, Q1, Q2, Q3, Q4]), "operationType" : NewBodyOperationType.ADD, "depth" : 16 * mm, "hasSecondDirection" : true, "secondDirectionOppositeDirection" : false, "secondDirectionDepth" : 1 * mm});
        }
        {
            var Q0;
            Q0=makeQuery(id+"F1.opExtrude","CAP_FACE",FACE,{"disambiguationData":[OSD([sQuery(id+"F0.wireOp",EDGE,"E0.bottom"),sQuery(id+"F0.wireOp",EDGE,"E0.top"),sQuery(id+"F0.wireOp",EDGE,"E5.bottom"),sQuery(id+"F0.wireOp",EDGE,"E5.top"),sQuery(id+"F0.wireOp",EDGE,"E5.left"),sQuery(id+"F0.wireOp",EDGE,"E5.right"),sQuery(id+"F0.wireOp",EDGE,"E8"),sQuery(id+"F0.wireOp",EDGE,"E9"),sQuery(id+"F0.wireOp",EDGE,"E10"),sQuery(id+"F0.wireOp",EDGE,"E11"),sQuery(id+"F0.wireOp",EDGE,"E12"),sQuery(id+"F0.wireOp",EDGE,"E14.MirrorCS"),sQuery(id+"F0.wireOp",EDGE,"E15.MirrorCS"),sQuery(id+"F0.wireOp",EDGE,"E16.MirrorCS"),sQuery(id+"F0.wireOp",EDGE,"E17.MirrorCS"),sQuery(id+"F0.wireOp",EDGE,"E18.MirrorCS")])],"isStart":false});
            var sketch = newSketch(context, id + "F26", { "sketchPlane" : qUnion([Q0])});
            skCircle(sketch, "E102", {"center": v(-14.13, 34.58) * mm, "radius": 3 * mm, "construction": true});
            skLineSegment(sketch, "E103", {"start": v(-14.13, 34.58) * mm, "end": v(-19.1, 34.58) * mm, "construction": true});
            skLineSegment(sketch, "E104", {"start": v(-17.13, 34.58) * mm, "end": v(-17.13, 52.78) * mm, "construction": true});
            skCircle(sketch, "E105", {"center": v(-17.13, 52.78) * mm, "radius": 7 * mm, "construction": true});
            skCircle(sketch, "E106", {"center": v(-17.13, 45.78) * mm, "radius": 3 * mm, "construction": true});
            skCircle(sketch, "E107", {"center": v(-17.13, 45.78) * mm, "radius": 1.2 * mm});
            skLineSegment(sketch, "E108.bottom", {"start": v(-20.13, 48.78) * mm, "end": v(-14.13, 48.78) * mm});
            skLineSegment(sketch, "E108.top", {"start": v(-20.13, 42.78) * mm, "end": v(-14.13, 42.78) * mm});
            skLineSegment(sketch, "E108.left", {"start": v(-20.13, 48.78) * mm, "end": v(-20.13, 42.78) * mm});
            skLineSegment(sketch, "E108.right", {"start": v(-14.13, 48.78) * mm, "end": v(-14.13, 42.78) * mm});
            skLineSegment(sketch, "E109", {"start": v(-49.88, -3.62) * mm, "end": v(-49.88, 0.08) * mm, "construction": true});
            skLineSegment(sketch, "E110", {"start": v(-49.88, 0.08) * mm, "end": v(-11.04, 0.08) * mm, "construction": true});
            skCircle(sketch, "E111", {"center": v(-14.13, 0.08) * mm, "radius": 12.2 * mm, "construction": true});
            skCircle(sketch, "E112", {"center": v(-26.33, 0.08) * mm, "radius": 1.2 * mm});
            skLineSegment(sketch, "E113.bottom", {"start": v(-28.83, 2.58) * mm, "end": v(-23.83, 2.58) * mm});
            skLineSegment(sketch, "E113.top", {"start": v(-28.83, -2.42) * mm, "end": v(-23.83, -2.42) * mm});
            skLineSegment(sketch, "E113.left", {"start": v(-28.83, 2.58) * mm, "end": v(-28.83, -2.42) * mm});
            skLineSegment(sketch, "E113.right", {"start": v(-23.83, 2.58) * mm, "end": v(-23.83, -2.42) * mm});
            skLineSegment(sketch, "E114", {"start": v(-55.13, -2.16) * mm, "end": v(-48.73, -2.16) * mm, "construction": true});
            skLineSegment(sketch, "E115", {"start": v(-48.73, -2.16) * mm, "end": v(-48.73, 60.43) * mm, "construction": true});
            skLineSegment(sketch, "E116", {"start": v(-48.73, -2.16) * mm, "end": v(-48.73, -6.57) * mm, "construction": true});
            skCircle(sketch, "E117", {"center": v(-48.73, -3.62) * mm, "radius": 17.9 * mm, "construction": true});
            skCircle(sketch, "E118", {"center": v(-48.73, 14.28) * mm, "radius": 1.2 * mm});
            skLineSegment(sketch, "E119.bottom", {"start": v(-46.23, 16.78) * mm, "end": v(-51.23, 16.78) * mm});
            skLineSegment(sketch, "E119.top", {"start": v(-46.23, 11.78) * mm, "end": v(-51.23, 11.78) * mm});
            skLineSegment(sketch, "E119.left", {"start": v(-46.23, 16.78) * mm, "end": v(-46.23, 11.78) * mm});
            skLineSegment(sketch, "E119.right", {"start": v(-51.23, 16.78) * mm, "end": v(-51.23, 11.78) * mm});
            skLineSegment(sketch, "E120", {"start": v(-17.13, 45.78) * mm, "end": v(-37.7, 45.78) * mm, "construction": true});
            skLineSegment(sketch, "E121.bottom", {"start": v(-34.7, 48.78) * mm, "end": v(-40.7, 48.78) * mm});
            skLineSegment(sketch, "E121.top", {"start": v(-34.7, 42.78) * mm, "end": v(-40.7, 42.78) * mm});
            skLineSegment(sketch, "E121.left", {"start": v(-34.7, 48.78) * mm, "end": v(-34.7, 42.78) * mm});
            skLineSegment(sketch, "E121.right", {"start": v(-40.7, 48.78) * mm, "end": v(-40.7, 42.78) * mm});
            skPoint(sketch, "E121.middle", {"position": v(-37.7, 45.78) * mm});
            skSolve(sketch);
        }
        {
            var Q0;
            Q0=makeQuery(id+"F26.imprint","IMPRINT",FACE,{"disambiguationData":[TD([[makeQuery(id+"F26.imprint","IMPRINT",EDGE,{"derivedFrom":sQuery(id+"F26.wireOp",EDGE,"E118")}),-1.0]])]});
            var Q1;
            Q1=makeQuery(id+"F26.imprint","IMPRINT",FACE,{"disambiguationData":[TD([[makeQuery(id+"F26.imprint","IMPRINT",EDGE,{"derivedFrom":sQuery(id+"F26.wireOp",EDGE,"E112")}),-1.0]])]});
            var Q2;
            Q2=makeQuery(id+"F26.imprint","IMPRINT",FACE,{"disambiguationData":[TD([[makeQuery(id+"F26.imprint","IMPRINT",EDGE,{"derivedFrom":sQuery(id+"F26.wireOp",EDGE,"E107")}),-1.0]])]});
            var Q3;
            Q3=makeQuery(id+"F26.imprint","IMPRINT",FACE,{"disambiguationData":[TD([[makeQuery(id+"F26.imprint","IMPRINT",EDGE,{"derivedFrom":sQuery(id+"F26.wireOp",EDGE,"E121.bottom")}),1.0]])]});
            extrude(context, id + "F27", {"entities" : qUnion([Q0, Q1, Q2, Q3]), "operationType" : NewBodyOperationType.ADD, "depth" : 4 * mm});
        }
    });
